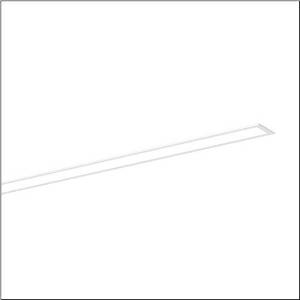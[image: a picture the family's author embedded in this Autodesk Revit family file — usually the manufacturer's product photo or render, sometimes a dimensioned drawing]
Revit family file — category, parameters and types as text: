
# Revit family: silica_r__21_51mx10tat2w_99a0
name_source: partatom
category: Lighting Fixtures
units: mm (PartAtom-declared; Revit-internal decimal feet)

## family parameters
Cut with Voids When Loaded = No
Host = Face
Light Source = No
Part Type = Normal
Room Calculation Point = No
Round Connector Dimension = Use Diameter
Shared = No

## types (1)
- --- (1 x LED, 2400 lm, 20.5 W, 6500K)
    Apparent Load = 21 VA
    CIE Flux Codes = 48 79 96 100 100
    Color Rendering = 80
    Color Temperature = 6500K
    Default Elevation = 1800 mm
    Description = Silica® 21, office luminaire, primary optical cover: cover, of PMMA, opal, light emission: direct distribution, primary light characteristic: symmetric, installation type: recessed, LED, rated luminous flux: 2.400lm, luminous efficacy: 112lm/W, light colour: 8tw, colour temperature: 2700..6500K, control gear: DALI DT8, with terminal, 3+2-pole, max. 2.5mm², mains connection: 220..240V, AC, 50/60Hz, rated input power: 21.5W, luminaire housing, of aluminium, traffic white (RAL 9016), length: 1.228mm, width: 79mm, height: 53mm, protection rating (complete): IP20, insulation class (complete): insulation class I (protective earthing), certification: CE, ENEC, VDE, permissible operating ambient temperature: 0..+35°C, standard: EN 50419, packaging unit: 1 piece
    Height = 0 mm  [stored 0 ft]
    Lamp = 1 x LED
    Lamp Light Flux = 2400 lm
    Lamp Power = 20.5 W
    Lamp count = 1
    Length = 1227 mm
    Luminous efficacy = 117 lm/W
    Manufacturer = Siteco
    ModVariant = No
    Model = 51MX10TAT2W
    Mounting Place = Ceiling
    Mounting Type = Recessed
    Number of Poles = 1
    OnlyDefault = Yes
    Power Factor = 1
    Product Name = Silica® 21
    Product group = office luminaire | ceiling recessed
    ProductGroupID = 401
    Protection Class = Protection class I
    Protection Degree = IP 20
    RLX_Detail_Level = 1
    RLX_Emergency_Light_Flux = 0 lm
    RLX_Emergency_Type = 0
    RLX_Emergency_Type_DB = No
    RlxData = <blob elided: 17941 chars, md5=a843a641>
    Socket = socket
    Standby Power = 0 W
    System Light Flux = 2400 lm
    System Power = 21 W
    Type Comments = individual setting
    Type Image = l_1335891.jpg
    URL = http://relux.com
    VarID = @adj_139728
    Voltage = 0 V
    Weight = 0.00 kg
    Width = 79 mm

note: [stored X ft] marks values corroborated as IEEE doubles in the binary element streams (Revit-internal decimal feet)

## geometry (parser evidence)
native form markers: Blend x4, Sweep x12
no freeform markers — native parametric forms only
